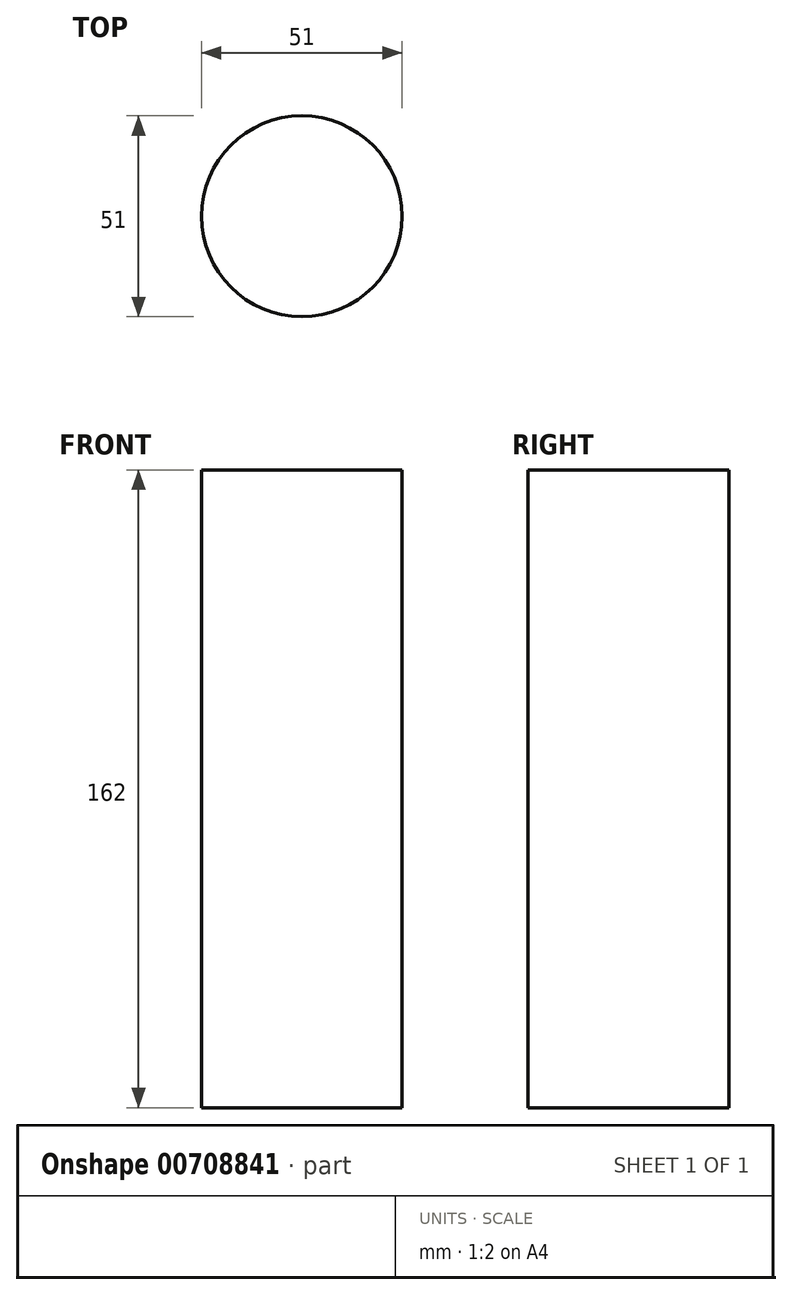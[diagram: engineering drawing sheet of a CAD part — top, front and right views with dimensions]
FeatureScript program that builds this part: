
annotation { "Feature Type Name" : "Feature", "Feature Type Description" : "" }
export const myFeature = defineFeature(function(context is Context, id is Id, definition is map)
    precondition{}
    {
        {
            var Q0;
            Q0=qCreatedBy(makeId("Top.planeOp"),FACE);
            var sketch = newSketch(context, id + "F0", { "sketchPlane" : qUnion([Q0])});
            skCircle(sketch, "E0", {"center": v(0, 0) * mm, "radius": 25.5 * mm});
            skSolve(sketch);
        }
        {
            var Q0;
            Q0=makeQuery(id+"F0.imprint","IMPRINT",FACE,{"disambiguationData":[TD([[makeQuery(id+"F0.imprint","IMPRINT",EDGE,{"derivedFrom":sQuery(id+"F0.wireOp",EDGE,"E0")}),1.0]])]});
            extrude(context, id + "F1", {"entities" : qUnion([Q0]), "depth" : 162 * mm, "offsetDistance" : 25 * mm});
        }
    });
